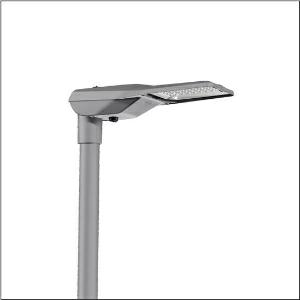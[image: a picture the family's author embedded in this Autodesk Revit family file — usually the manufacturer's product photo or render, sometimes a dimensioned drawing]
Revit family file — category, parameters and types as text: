
# Revit family: streetlight_sl_21_iq_mini___st1_0a_5xe2d21y08jb_5dbb
name_source: partatom
category: Lighting Fixtures
units: mm (PartAtom-declared; Revit-internal decimal feet)

## family parameters
Cut with Voids When Loaded = No
Host = Face
Light Source = No
Part Type = Normal
Room Calculation Point = No
Round Connector Dimension = Use Diameter
Shared = No

## types (1)
- --- (1 x LED, 9000 lm, 72.5 W, 2200K)
    Apparent Load = 73 VA
    CIE Flux Codes = 40 73 97 100 100
    Color Rendering = 70
    Color Temperature = 2200K
    Default Elevation = 1800 mm
    Description = Streetlight SL 21 iQ mini, mast luminaire, primary light control with lens, of PMMA, primary optical cover: cover, of toughened safety glass, transparent, light distribution: ST1.0a, light emission: direct distribution, primary light characteristic: asymmetric, installation type: post-top, side-entry, LED, High Power LED, rated luminous flux: 9.000lm, luminous efficacy: 124lm/W, light colour: 722, colour temperature: 2200K, control: presetting dimming logarithmic, Street-Remote, Auto-Match, Temp-Guard, Lumen-Switch, Night-Set, Smart-Wire, Light-Fading, Desk-Remote (wireless, voltage-free reading and setting of iQ features in the workshop via application-optimized NFC function/RFID function), optimised constant luminous flux control (CLO 2.0), mains connection: 220..240V, AC, 50/60Hz, start of lifetime: 73W, end of service life: 76W, reduction: 33W, luminaire housing, of diecast aluminium, powder-coated, Siteco® metallic grey (DB 702S), corrosivity category C5 mid according to DIN EN ISO 12944, please order mast flange separately, inclination adjustable: 0°, 5°, 10°, 15°, sealing non-destructively replaceable, multi-level sealing system, length: 628mm, width: 235mm, height: 110mm, mast flange for spigot size: 42mm (side-entry): 5XC10008XM4, 60/48mm (side-entry/post-top): 5XC10108XM2, 76/60mm (side-entry/post-top): 5XC10108XM1, Smart Interface below and above, protection rating (complete): IP66, insulation class (complete): insulation class II (safety insulation), certification: CE, ENEC, ENEC+, VDE, impact resistance: IK09, permissible operating ambient temperature for outdoor applications: -40..+50°C, standard-compliant lighting for roads and squares, packaging unit: 1 piece

Light Distribution: ST1.0a
    Height = 110 mm
    Lamp = 1 x LED
    Lamp Light Flux = 9000 lm
    Lamp Power = 72.5 W
    Lamp count = 1
    Length = 625 mm
    Luminous efficacy = 124 lm/W
    Manufacturer = Siteco
    ModVariant = No
    Model = 5XE2D21Y08JB
    Number of Poles = 1
    OnlyDefault = Yes
    Power Factor = 1
    Product Name = Streetlight SL 21 iQ mini | ST1.0a
    Product group = mast luminaire | pylon top
    ProductGroupID = 6100
    Protection Class = Protection class II
    Protection Degree = IP 66
    RLX_Detail_Level = 1
    RLX_Emergency_Light_Flux = 0 lm
    RLX_Emergency_Type = 0
    RLX_Emergency_Type_DB = No
    RlxData = <blob elided: 92429 chars, md5=67c83f71>
    Socket = socket
    Standby Power = 0 W
    System Light Flux = 9000 lm
    System Power = 73 W
    Type Comments = factory setting: luminous flux: 100 % | dim-lin: 254 | 755 mA
    Type Image = l_1003514.jpg
    URL = http://relux.com
    VarID = @adj_044187
    Voltage = 0 V
    Weight = 0.00 kg
    Width = 234 mm

## geometry (parser evidence)
native form markers: Blend x4, Sweep x10
no freeform markers — native parametric forms only
